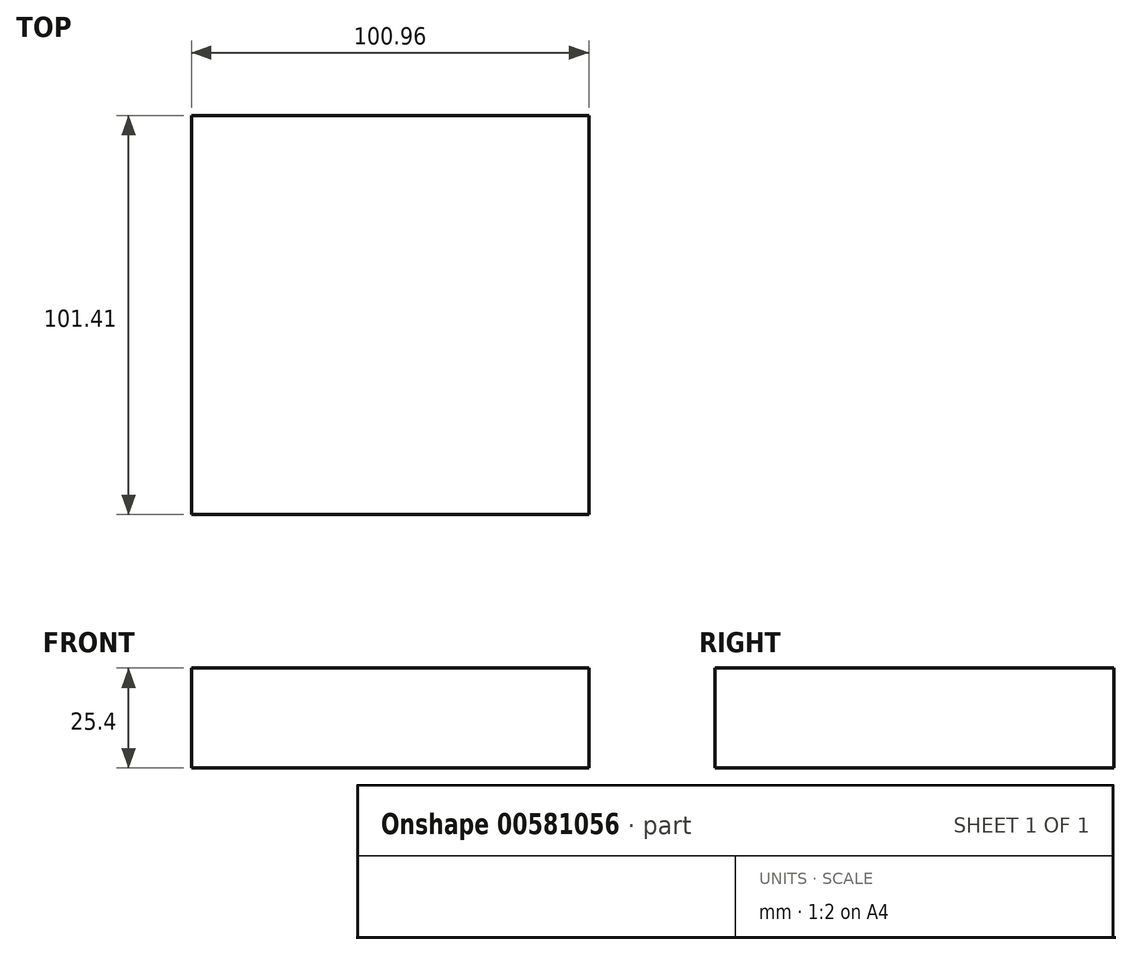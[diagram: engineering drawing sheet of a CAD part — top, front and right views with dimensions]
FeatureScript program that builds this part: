
annotation { "Feature Type Name" : "Feature", "Feature Type Description" : "" }
export const myFeature = defineFeature(function(context is Context, id is Id, definition is map)
    precondition{}
    {
        {
            var Q0;
            Q0=qCreatedBy(makeId("Top.planeOp"),FACE);
            var sketch = newSketch(context, id + "F0", { "sketchPlane" : qUnion([Q0])});
            skLineSegment(sketch, "E0.bottom", {"start": v(-47.44, 51.24) * mm, "end": v(53.52, 51.24) * mm});
            skLineSegment(sketch, "E0.top", {"start": v(-47.44, -50.17) * mm, "end": v(53.52, -50.17) * mm});
            skLineSegment(sketch, "E0.left", {"start": v(-47.44, 51.24) * mm, "end": v(-47.44, -50.17) * mm});
            skLineSegment(sketch, "E0.right", {"start": v(53.52, 51.24) * mm, "end": v(53.52, -50.17) * mm});
            skSolve(sketch);
        }
        {
            var Q0;
            Q0=makeQuery(id+"F0.imprint","IMPRINT",FACE,{"disambiguationData":[TD([[makeQuery(id+"F0.imprint","IMPRINT",EDGE,{"derivedFrom":sQuery(id+"F0.wireOp",EDGE,"E0.bottom")}),-1.0]])]});
            extrude(context, id + "F1", {"entities" : qUnion([Q0]), "depth" : 25.4 * mm, "offsetDistance" : 25.4 * mm});
        }
    });
